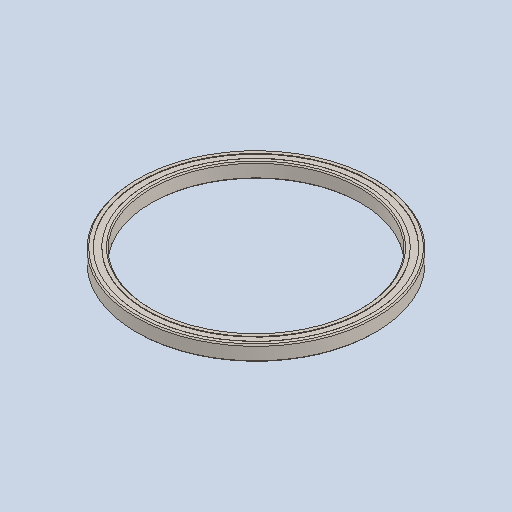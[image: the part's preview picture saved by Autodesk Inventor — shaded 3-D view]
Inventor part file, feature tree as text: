
AUTODESK INVENTOR PART (.ipt)
format: ipt  version: 2024.2 (Build 282272000, 272)  size: 128,512 bytes
history: native  units: in
note: dims shown in document units (in); Inventor stores cm internally (conversion verified against a paired STEP export)
features: revolve x1
ambient origin geometry x8: Origin, YZ Plane, XZ Plane, XY Plane, X Axis, Y Axis, Z Axis, Center Point
bodies: Solid1 (feature_tree)
feature tree (1):
  revolve  "Revolve1"  [1 undecoded]
note: 1 required parameter value undecoded (feature->parameter linkage not recoverable at this tier; creation-order binding heuristic only, values carry confidence <= 0.55)
